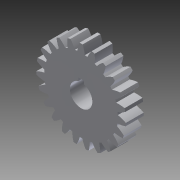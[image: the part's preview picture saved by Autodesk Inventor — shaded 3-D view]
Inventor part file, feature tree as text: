
AUTODESK INVENTOR PART (.ipt)
format: ipt  version: 2013 (Build 170138000, 138)  size: 222,208 bytes
history: native  units: in
note: dims shown in document units (in); Inventor stores cm internally (conversion verified against a paired STEP export)
features: extrude x1, sketch x1
ambient origin geometry x8: Origin, YZ Plane, XZ Plane, XY Plane, X Axis, Y Axis, Z Axis, Center Point
bodies: Solid1 (feature_tree)
feature tree (2):
  extrude  "Extrusion1"  Depth=0.0394in
  sketch  "Sketch1"  dims[d0=0.315in d1=0.0394in d2=0.0394in d3=0.0394in d4=0.25in d5=0.0in]
